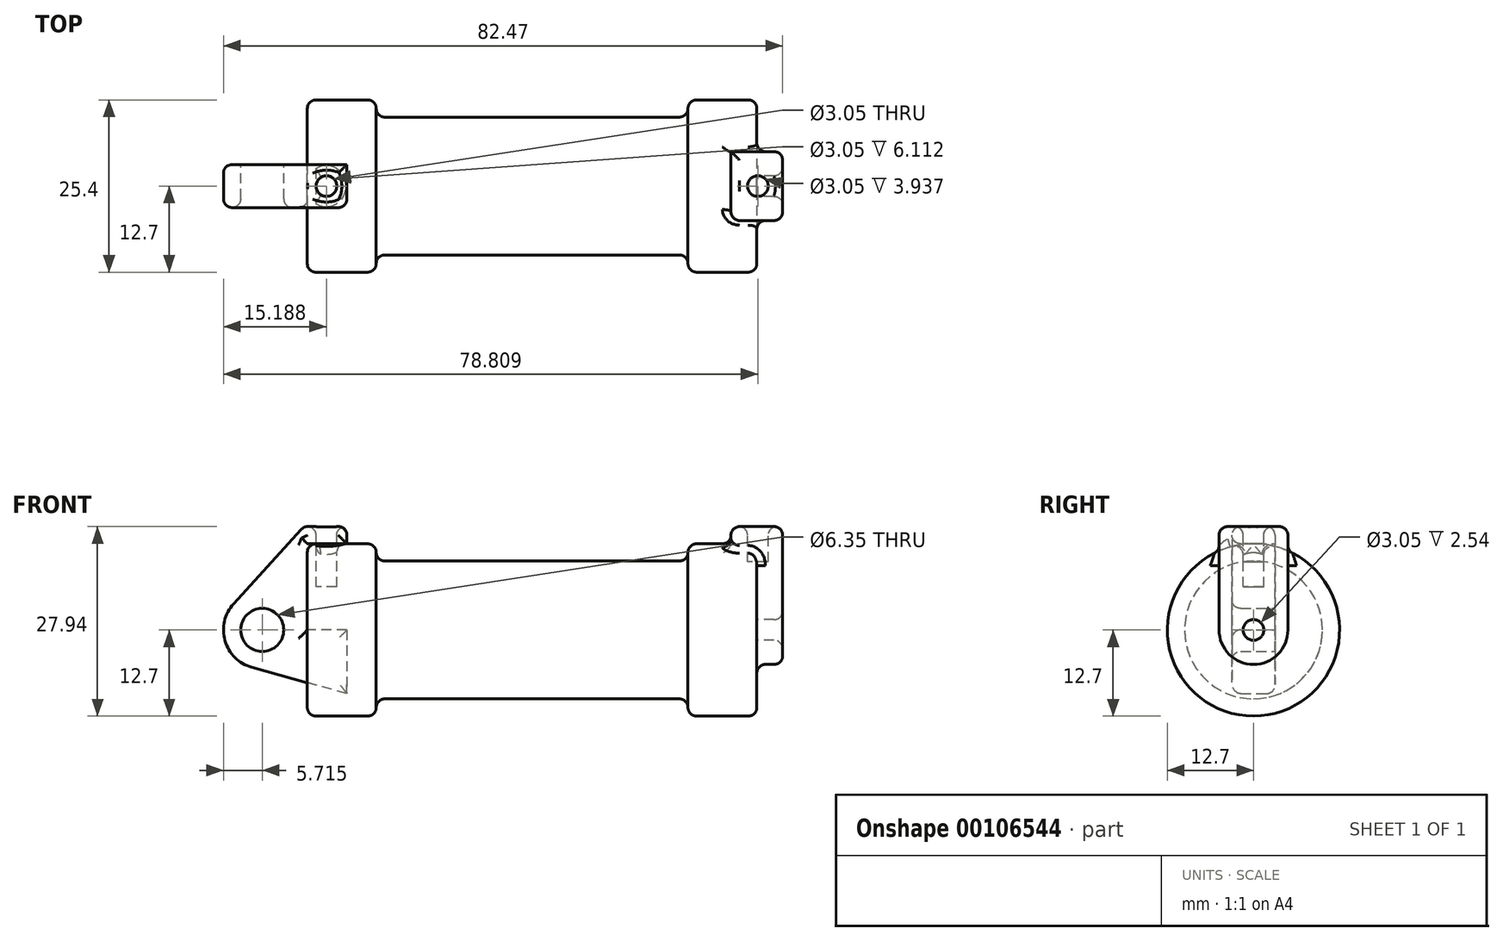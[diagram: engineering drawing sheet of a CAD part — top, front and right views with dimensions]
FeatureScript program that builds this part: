
annotation { "Feature Type Name" : "Feature", "Feature Type Description" : "" }
export const myFeature = defineFeature(function(context is Context, id is Id, definition is map)
    precondition{}
    {
        {
            var Q0;
            Q0=qCreatedBy(makeId("Front.planeOp"),FACE);
            var sketch = newSketch(context, id + "F0", { "sketchPlane" : qUnion([Q0])});
            skLineSegment(sketch, "E0", {"start": v(0, 0) * mm, "end": v(0, 12.7) * mm});
            skLineSegment(sketch, "E1", {"start": v(0, 12.7) * mm, "end": v(10.16, 12.7) * mm});
            skLineSegment(sketch, "E2", {"start": v(10.16, 12.7) * mm, "end": v(10.16, 10.16) * mm});
            skLineSegment(sketch, "E3", {"start": v(10.16, 10.16) * mm, "end": v(56.13, 10.16) * mm});
            skLineSegment(sketch, "E4", {"start": v(56.13, 10.16) * mm, "end": v(56.13, 12.7) * mm});
            skLineSegment(sketch, "E5", {"start": v(56.13, 12.7) * mm, "end": v(66.3, 12.7) * mm});
            skLineSegment(sketch, "E6", {"start": v(66.3, 12.7) * mm, "end": v(66.3, 0) * mm});
            skLineSegment(sketch, "E7", {"start": v(66.3, 0) * mm, "end": v(0, 0) * mm});
            skLineSegment(sketch, "E8", {"start": v(5.84, 15.24) * mm, "end": v(-0.5, 15.24) * mm});
            skLineSegment(sketch, "E9", {"start": v(-0.5, 15.24) * mm, "end": v(-10.88, 3.85) * mm});
            skLineSegment(sketch, "E10", {"start": v(0, 0) * mm, "end": v(-6.65, 0) * mm});
            skCircle(sketch, "E11", {"center": v(-6.65, 0) * mm, "radius": 5.72 * mm});
            skCircle(sketch, "E12", {"center": v(-6.65, 0) * mm, "radius": 3.18 * mm});
            skLineSegment(sketch, "E13", {"start": v(5.84, 15.24) * mm, "end": v(5.84, -9.4) * mm});
            skLineSegment(sketch, "E14", {"start": v(5.84, -9.4) * mm, "end": v(-8.18, -5.5) * mm});
            skSolve(sketch);
        }
        {
            var Q0;
            {var subQ0=sQuery(id+"F0.wireOp",EDGE,"E0");Q0=makeQuery(id+"F0.imprint","IMPRINT",FACE,{"disambiguationData":[TD([[makeQuery(id+"F0.imprint","IMPRINT",EDGE,{"derivedFrom":subQ0}),-1.0]])]});}
            var Q1;
            {var subQ0=sQuery(id+"F0.wireOp",EDGE,"E2");Q1=makeQuery(id+"F0.imprint","IMPRINT",FACE,{"disambiguationData":[TD([[makeQuery(id+"F0.imprint","IMPRINT",EDGE,{"derivedFrom":subQ0}),-1.0]])]});}
            var Q2;
            Q2=sQuery(id+"F0.wireOp",EDGE,"E7");
            revolve(context, id + "F1", {"entities" : qUnion([Q0, Q1]), "axis" : qUnion([Q2]), "revolveType" : RevolveType.FULL});
        }
        {
            var Q0;
            {var subQ3=sQuery(id+"F0.wireOp",EDGE,"E0");Q0=makeQuery(id+"F0.imprint","IMPRINT",FACE,{"disambiguationData":[TD([[makeQuery(id+"F0.imprint","IMPRINT",EDGE,{"derivedFrom":subQ3}),1.0]])]});}
            var Q1;
            {var subQ0=sQuery(id+"F0.wireOp",EDGE,"E14");Q1=makeQuery(id+"F0.imprint","IMPRINT",FACE,{"disambiguationData":[TD([[makeQuery(id+"F0.imprint","IMPRINT",EDGE,{"derivedFrom":subQ0}),-1.0]])]});}
            var Q2;
            {var subQ4=sQuery(id+"F0.wireOp",EDGE,"E12");Q2=makeQuery(id+"F0.imprint","IMPRINT",FACE,{"disambiguationData":[TD([[makeQuery(id+"F0.imprint","IMPRINT",EDGE,{"derivedFrom":subQ4}),-1.0]])]});}
            extrude(context, id + "F2", {"entities" : qUnion([Q0, Q1, Q2]), "endBound" : BoundingType.SYMMETRIC, "depth" : 6.35 * mm});
        }
        {
            var Q0;
            Q0=makeQuery(id+"F1.opRevolve","SWEPT_FACE",FACE,{"disambiguationData":[OSD([sQuery(id+"F0.wireOp",EDGE,"E6")])]});
            var sketch = newSketch(context, id + "F3", { "sketchPlane" : qUnion([Q0])});
            skCircle(sketch, "E15", {"center": v(0, 0) * mm, "radius": 5.08 * mm});
            skCircle(sketch, "E16", {"center": v(0, 0) * mm, "radius": 1.52 * mm});
            skLineSegment(sketch, "E17", {"start": v(-5.08, 15.24) * mm, "end": v(-5.08, 0) * mm});
            skLineSegment(sketch, "E18", {"start": v(5.08, 15.24) * mm, "end": v(5.08, 0) * mm});
            skLineSegment(sketch, "E19", {"start": v(-5.08, 15.24) * mm, "end": v(5.08, 15.24) * mm});
            skSolve(sketch);
        }
        {
            var Q0;
            Q0 = qSketchRegion(id + "F3", true);
            extrude(context, id + "F4", {"entities" : qUnion([Q0]), "operationType" : NewBodyOperationType.ADD, "endBound" : BoundingType.SYMMETRIC, "depth" : 7.62 * mm});
        }
        {
            var Q0;
            Q0=makeQuery(id+"F4.opExtrude","SWEPT_FACE",FACE,{"disambiguationData":[OSD([sQuery(id+"F3.wireOp",EDGE,"E19")])]});
            var sketch = newSketch(context, id + "F5", { "sketchPlane" : qUnion([Q0])});
            skCircle(sketch, "E20", {"center": v(66.44, 0) * mm, "radius": 1.52 * mm});
            skPoint(sketch, "E20.centerSnap0", {"position": v(62.48, 0) * mm});
            skSolve(sketch);
        }
        {
            var Q0;
            Q0=makeQuery(id+"F2.opExtrude","SWEPT_FACE",FACE,{"disambiguationData":[OSD([sQuery(id+"F0.wireOp",EDGE,"E8")])]});
            var sketch = newSketch(context, id + "F6", { "sketchPlane" : qUnion([Q0])});
            skCircle(sketch, "E21", {"center": v(2.82, 0) * mm, "radius": 1.52 * mm});
            skSolve(sketch);
        }
        {
            var Q0;
            Q0=makeQuery(id+"F6.imprint","IMPRINT",FACE,{"disambiguationData":[TD([[makeQuery(id+"F6.imprint","IMPRINT",EDGE,{"derivedFrom":sQuery(id+"F6.wireOp",EDGE,"E21")}),1.0]])]});
            extrude(context, id + "F7", {"entities" : qUnion([Q0]), "operationType" : NewBodyOperationType.REMOVE, "endBound" : BoundingType.SYMMETRIC, "oppositeDirection" : true, "depth" : 17.78 * mm});
        }
        {
            var Q0;
            Q0=makeQuery(id+"F5.imprint","IMPRINT",FACE,{"disambiguationData":[TD([[makeQuery(id+"F5.imprint","IMPRINT",EDGE,{"derivedFrom":sQuery(id+"F5.wireOp",EDGE,"E20")}),1.0]])]});
            extrude(context, id + "F8", {"entities" : qUnion([Q0]), "operationType" : NewBodyOperationType.REMOVE, "endBound" : BoundingType.SYMMETRIC, "oppositeDirection" : true, "depth" : 10.4 * mm});
        }
        {
            var Q0;
            Q0=makeQuery(id+"F1.opRevolve","SWEPT_EDGE",EDGE,{"disambiguationData":[OSD([sQuery(id+"F0.wireOp",EDGE,"E1"),sQuery(id+"F0.wireOp",EDGE,"E2")])]});
            var Q1;
            Q1=makeQuery(id+"F1.opRevolve","SWEPT_EDGE",EDGE,{"disambiguationData":[OSD([sQuery(id+"F0.wireOp",EDGE,"E2"),sQuery(id+"F0.wireOp",EDGE,"E3")])]});
            var Q2;
            Q2=makeQuery(id+"F1.opRevolve","SWEPT_EDGE",EDGE,{"disambiguationData":[OSD([sQuery(id+"F0.wireOp",EDGE,"E5"),sQuery(id+"F0.wireOp",EDGE,"E6")])]});
            fillet(context, id + "F9", {"entities" : qUnion([Q0, Q1, Q2]), "radius" : 1.27 * mm, "tangentPropagation" : true, "allowEdgeOverflow" : false});
        }
        {
            var Q0;
            Q0=makeQuery(id+"F1.opRevolve","SWEPT_EDGE",EDGE,{"disambiguationData":[OSD([sQuery(id+"F0.wireOp",EDGE,"E0"),sQuery(id+"F0.wireOp",EDGE,"E1")])]});
            var Q1;
            Q1=makeQuery(id+"F1.opRevolve","SWEPT_EDGE",EDGE,{"disambiguationData":[OSD([sQuery(id+"F0.wireOp",EDGE,"E4"),sQuery(id+"F0.wireOp",EDGE,"E5")])]});
            fillet(context, id + "F10", {"entities" : qUnion([Q0, Q1]), "radius" : 1.27 * mm, "tangentPropagation" : true, "allowEdgeOverflow" : false});
        }
        {
            var Q0;
            Q0=makeQuery(id+"F1.opRevolve","SWEPT_FACE",FACE,{"disambiguationData":[OSD([sQuery(id+"F0.wireOp",EDGE,"E3")])]});
            var Q1;
            Q1=makeQuery(id+"F1.opRevolve","SWEPT_FACE",FACE,{"disambiguationData":[OSD([sQuery(id+"F0.wireOp",EDGE,"E1")])]});
            var Q2;
            Q2=makeQuery(id+"F2.opExtrude","SWEPT_FACE",FACE,{"disambiguationData":[OSD([sQuery(id+"F0.wireOp",EDGE,"E9")])]});
            var Q3;
            Q3=makeQuery(id+"F2.opExtrude","CAP_FACE",FACE,{"disambiguationData":[OSD([sQuery(id+"F0.wireOp",EDGE,"E0"),sQuery(id+"F0.wireOp",EDGE,"E1"),sQuery(id+"F0.wireOp",EDGE,"E7"),sQuery(id+"F0.wireOp",EDGE,"E8"),sQuery(id+"F0.wireOp",EDGE,"E9"),sQuery(id+"F0.wireOp",EDGE,"E11"),sQuery(id+"F0.wireOp",EDGE,"E12"),sQuery(id+"F0.wireOp",EDGE,"E13"),sQuery(id+"F0.wireOp",EDGE,"E14")])],"isStart":false});
            var Q4;
            Q4=makeQuery(id+"F2.opExtrude","SWEPT_FACE",FACE,{"disambiguationData":[OSD([sQuery(id+"F0.wireOp",EDGE,"E11")])]});
            var Q5;
            Q5=makeQuery(id+"F1.opRevolve","SWEPT_FACE",FACE,{"disambiguationData":[OSD([sQuery(id+"F0.wireOp",EDGE,"E5")])]});
            var Q6;
            Q6=makeQuery(id+"F4.boolean.opBoolean","SPLIT",FACE,{"disambiguationData":[TD([makeQuery(id+"F1.opRevolve","SWEPT_FACE",FACE,{"disambiguationData":[OSD([sQuery(id+"F0.wireOp",EDGE,"E5")])]})])],"derivedFrom":makeQuery(id+"F1.opRevolve","SWEPT_FACE",FACE,{"disambiguationData":[OSD([sQuery(id+"F0.wireOp",EDGE,"E6")])]})});
            var Q7;
            {var subQ0=sQuery(id+"F0.wireOp",EDGE,"E5");Q7=makeQuery(id+"F9.opFillet","BLEND_EDGE",EDGE,{"blendedFrom":[makeQuery(id+"F1.opRevolve","SWEPT_EDGE",EDGE,{"disambiguationData":[OSD([subQ0,sQuery(id+"F0.wireOp",EDGE,"E6")])]}),makeQuery(id+"F1.opRevolve","SWEPT_FACE",FACE,{"disambiguationData":[OSD([subQ0])]})],"blendedInto":[makeQuery(id+"F1.opRevolve","SWEPT_FACE",FACE,{"disambiguationData":[OSD([subQ0])]})]});}
            var Q8;
            Q8=makeQuery(id+"F4.opExtrude","CAP_FACE",FACE,{"disambiguationData":[OSD([sQuery(id+"F3.wireOp",EDGE,"E15"),sQuery(id+"F3.wireOp",EDGE,"E16"),sQuery(id+"F3.wireOp",EDGE,"E17"),sQuery(id+"F3.wireOp",EDGE,"E18"),sQuery(id+"F3.wireOp",EDGE,"E19")])],"isStart":false});
            var Q9;
            Q9=makeQuery(id+"F4.opExtrude","SWEPT_FACE",FACE,{"disambiguationData":[OSD([sQuery(id+"F3.wireOp",EDGE,"E17")])]});
            var Q10;
            Q10=makeQuery(id+"F4.opExtrude","SWEPT_FACE",FACE,{"disambiguationData":[OSD([sQuery(id+"F3.wireOp",EDGE,"E19")])]});
            var Q11;
            Q11=makeQuery(id+"F2.opExtrude","SWEPT_FACE",FACE,{"disambiguationData":[OSD([sQuery(id+"F0.wireOp",EDGE,"E8")])]});
            fillet(context, id + "F11", {"entities" : qUnion([Q0, Q1, Q2, Q3, Q4, Q5, Q6, Q7, Q8, Q9, Q10, Q11]), "radius" : 1.27 * mm, "tangentPropagation" : true, "allowEdgeOverflow" : false});
        }
    });
